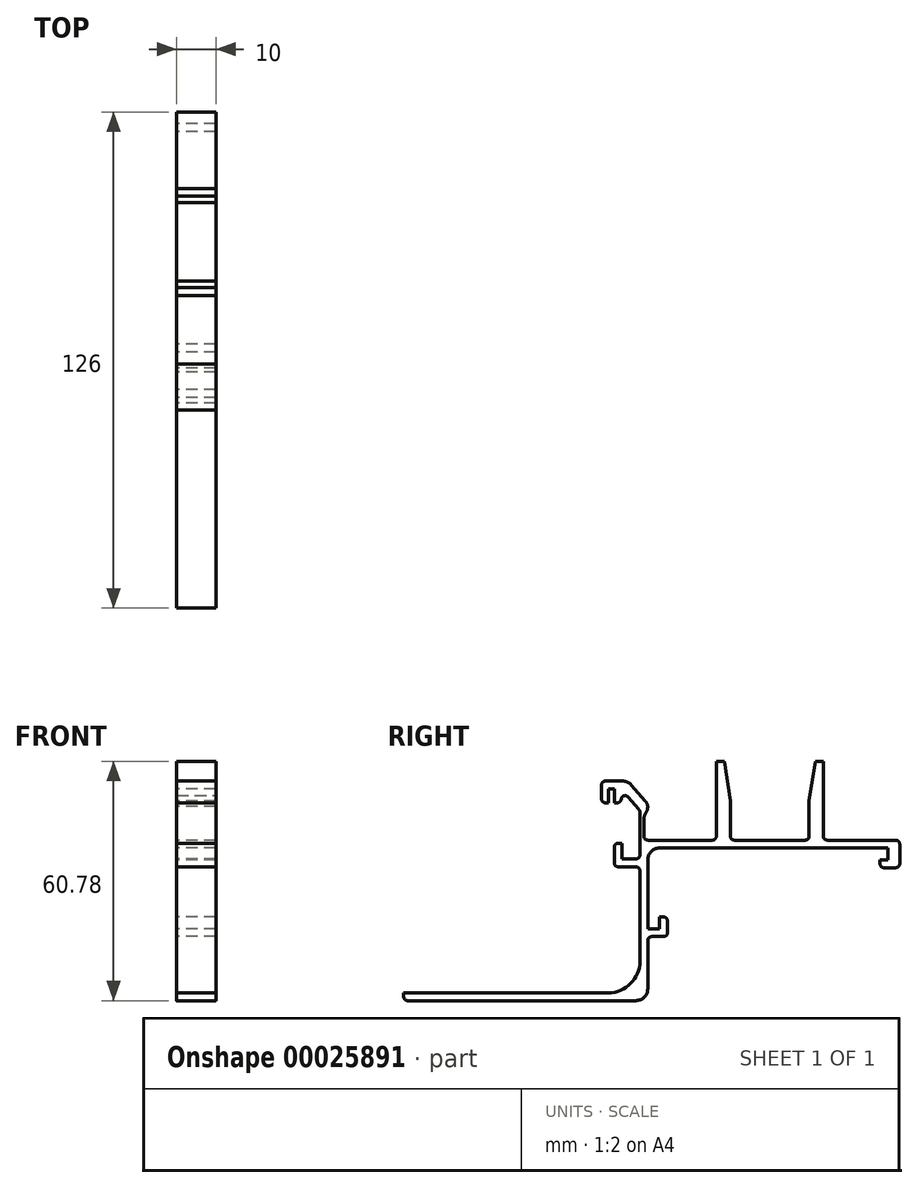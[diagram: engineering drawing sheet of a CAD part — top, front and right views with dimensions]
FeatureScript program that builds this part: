
annotation { "Feature Type Name" : "Feature", "Feature Type Description" : "" }
export const myFeature = defineFeature(function(context is Context, id is Id, definition is map)
    precondition{}
    {
        {
            var Q0;
            Q0=qCreatedBy(makeId("Right.planeOp"),FACE);
            var sketch = newSketch(context, id + "F0", { "sketchPlane" : qUnion([Q0])});
            skLineSegment(sketch, "E0", {"start": v(-5, 35.7) * mm, "end": v(56, 35.7) * mm});
            skLineSegment(sketch, "E1", {"start": v(56, 35.7) * mm, "end": v(56, 32.7) * mm});
            skLineSegment(sketch, "E2", {"start": v(56, 32.7) * mm, "end": v(54, 32.7) * mm});
            skLineSegment(sketch, "E3", {"start": v(54, 32.7) * mm, "end": v(54, 30.7) * mm});
            skLineSegment(sketch, "E4", {"start": v(54, 30.7) * mm, "end": v(59, 30.7) * mm});
            skLineSegment(sketch, "E5", {"start": v(59, 30.7) * mm, "end": v(59, 37.7) * mm});
            skLineSegment(sketch, "E6", {"start": v(59, 37.7) * mm, "end": v(-7, 37.7) * mm});
            skLineSegment(sketch, "E7", {"start": v(-5, 35.7) * mm, "end": v(-5, 15.2) * mm});
            skLineSegment(sketch, "E8", {"start": v(-7, 37.7) * mm, "end": v(-7, 17.59) * mm});
            skLineSegment(sketch, "E9", {"start": v(-5, 15.2) * mm, "end": v(-2, 15.2) * mm});
            skLineSegment(sketch, "E10", {"start": v(-2, 15.2) * mm, "end": v(-2, 18.2) * mm});
            skLineSegment(sketch, "E11", {"start": v(-2, 18.2) * mm, "end": v(0, 18.2) * mm});
            skLineSegment(sketch, "E12", {"start": v(0, 18.2) * mm, "end": v(0, 13.2) * mm});
            skLineSegment(sketch, "E13", {"start": v(0, 13.2) * mm, "end": v(-7, 13.2) * mm});
            skLineSegment(sketch, "E14", {"start": v(-7, 13.2) * mm, "end": v(-7, 17.59) * mm});
            skLineSegment(sketch, "E15", {"start": v(-5, 13.2) * mm, "end": v(-5, -3.82) * mm});
            skLineSegment(sketch, "E16", {"start": v(-7, -1.08) * mm, "end": v(-7, 13.2) * mm});
            skLineSegment(sketch, "E17", {"start": v(-7, 30.92) * mm, "end": v(-13.5, 30.92) * mm});
            skLineSegment(sketch, "E18", {"start": v(-13.5, 30.92) * mm, "end": v(-13.5, 36.92) * mm});
            skLineSegment(sketch, "E19", {"start": v(-13.5, 36.92) * mm, "end": v(-11.5, 36.92) * mm});
            skLineSegment(sketch, "E20", {"start": v(-11.5, 36.92) * mm, "end": v(-11.5, 32.92) * mm});
            skLineSegment(sketch, "E21", {"start": v(-11.5, 32.92) * mm, "end": v(-7, 32.92) * mm});
            skLineSegment(sketch, "E22", {"start": v(-7, -1.08) * mm, "end": v(-67, -1.08) * mm});
            skLineSegment(sketch, "E23", {"start": v(-5, -1.08) * mm, "end": v(-5, -3.82) * mm});
            skLineSegment(sketch, "E24", {"start": v(-67, -1.08) * mm, "end": v(-67, -3.08) * mm});
            skLineSegment(sketch, "E25", {"start": v(-67, -3.08) * mm, "end": v(-5, -3.08) * mm});
            skLineSegment(sketch, "E26", {"start": v(-5, -3.08) * mm, "end": v(-5, -1.08) * mm});
            skLineSegment(sketch, "E27", {"start": v(-62, -1.08) * mm, "end": v(-62, 4.95) * mm, "construction": true});
            skLineSegment(sketch, "E28", {"start": v(-7, 37.7) * mm, "end": v(-7, 49.25) * mm});
            skLineSegment(sketch, "E29", {"start": v(-8.26, 50.7) * mm, "end": v(-15, 50.7) * mm});
            skLineSegment(sketch, "E30", {"start": v(-15, 50.7) * mm, "end": v(-15, 47.2) * mm});
            skLineSegment(sketch, "E31", {"start": v(-15, 47.2) * mm, "end": v(-16.75, 47.2) * mm});
            skLineSegment(sketch, "E32", {"start": v(-16.75, 47.2) * mm, "end": v(-16.75, 52.7) * mm});
            skLineSegment(sketch, "E33", {"start": v(-16.75, 52.7) * mm, "end": v(-10, 52.7) * mm});
            skLineSegment(sketch, "E34", {"start": v(-7, 45.2) * mm, "end": v(-6, 45.2) * mm});
            skLineSegment(sketch, "E35", {"start": v(-6, 45.2) * mm, "end": v(-6, 37.7) * mm});
            skLineSegment(sketch, "E36", {"start": v(-5, 46.93) * mm, "end": v(-5, 45.2) * mm});
            skLineSegment(sketch, "E37", {"start": v(-5, 45.2) * mm, "end": v(-6, 45.2) * mm});
            skLineSegment(sketch, "E38", {"start": v(-11.75, 50.7) * mm, "end": v(-7, 45.2) * mm});
            skLineSegment(sketch, "E39", {"start": v(-7, 45.2) * mm, "end": v(-5, 46.93) * mm});
            skLineSegment(sketch, "E40", {"start": v(-5, 46.93) * mm, "end": v(-10, 52.7) * mm});
            skPoint(sketch, "E41.start.orphan", {"position": v(-7, 52.7) * mm});
            skLineSegment(sketch, "E42", {"start": v(-13.5, 50.7) * mm, "end": v(-13.5, 47.2) * mm});
            skLineSegment(sketch, "E43", {"start": v(-13.5, 47.2) * mm, "end": v(-11.75, 47.2) * mm});
            skLineSegment(sketch, "E44", {"start": v(-11.75, 47.2) * mm, "end": v(-11.75, 50.7) * mm});
            skLineSegment(sketch, "E45", {"start": v(26, 37.7) * mm, "end": v(26, 54.51) * mm, "construction": true});
            skLineSegment(sketch, "E46", {"start": v(16, 37.7) * mm, "end": v(16, 47.7) * mm});
            skLineSegment(sketch, "E47", {"start": v(16, 47.7) * mm, "end": v(14.42, 57.7) * mm});
            skLineSegment(sketch, "E48", {"start": v(14.42, 57.7) * mm, "end": v(12.42, 57.7) * mm});
            skLineSegment(sketch, "E49", {"start": v(12.42, 57.7) * mm, "end": v(12.42, 37.7) * mm});
            skLineSegment(sketch, "E50.MirrorCS", {"start": v(37.58, 57.7) * mm, "end": v(39.58, 57.7) * mm});
            skLineSegment(sketch, "E51.MirrorCS", {"start": v(36, 37.7) * mm, "end": v(36, 47.7) * mm});
            skLineSegment(sketch, "E52.MirrorCS", {"start": v(36, 47.7) * mm, "end": v(37.58, 57.7) * mm});
            skLineSegment(sketch, "E53.MirrorCS", {"start": v(39.58, 57.7) * mm, "end": v(39.58, 37.7) * mm});
            skSolve(sketch);
        }
        {
            var Q0;
            Q0=qSketchRegion(id+"F0",true);
            extrude(context, id + "F1", {"entities" : qUnion([Q0]), "depth" : 10 * mm});
        }
        {
            var Q0;
            Q0=makeQuery(id+"F1.opExtrude","SWEPT_EDGE",EDGE,{"disambiguationData":[OSD([sQuery(id+"F0.wireOp",EDGE,"E0"),sQuery(id+"F0.wireOp",EDGE,"E7")])]});
            fillet(context, id + "F2", {"entities" : qUnion([Q0]), "radius" : 3 * mm, "tangentPropagation" : true, "allowEdgeOverflow" : false});
        }
        {
            var Q0;
            Q0=makeQuery(id+"F1.opExtrude","SWEPT_EDGE",EDGE,{"disambiguationData":[OSD([sQuery(id+"F0.wireOp",EDGE,"E6"),sQuery(id+"F0.wireOp",EDGE,"E8")])]});
            var Q1;
            Q1=makeQuery(id+"F1.opExtrude","SWEPT_EDGE",EDGE,{"disambiguationData":[OSD([sQuery(id+"F0.wireOp",EDGE,"E13"),sQuery(id+"F0.wireOp",EDGE,"E14")])]});
            var Q2;
            Q2=makeQuery(id+"F1.opExtrude","SWEPT_EDGE",EDGE,{"disambiguationData":[OSD([sQuery(id+"F0.wireOp",EDGE,"E12"),sQuery(id+"F0.wireOp",EDGE,"E13")])]});
            var Q3;
            Q3=makeQuery(id+"F1.opExtrude","SWEPT_EDGE",EDGE,{"disambiguationData":[OSD([sQuery(id+"F0.wireOp",EDGE,"E5"),sQuery(id+"F0.wireOp",EDGE,"E6")])]});
            var Q4;
            Q4=makeQuery(id+"F1.opExtrude","SWEPT_EDGE",EDGE,{"disambiguationData":[OSD([sQuery(id+"F0.wireOp",EDGE,"E4"),sQuery(id+"F0.wireOp",EDGE,"E5")])]});
            var Q5;
            Q5=makeQuery(id+"F1.opExtrude","SWEPT_EDGE",EDGE,{"disambiguationData":[OSD([sQuery(id+"F0.wireOp",EDGE,"E3"),sQuery(id+"F0.wireOp",EDGE,"E4")])]});
            var Q6;
            Q6=makeQuery(id+"F1.opExtrude","SWEPT_EDGE",EDGE,{"disambiguationData":[OSD([sQuery(id+"F0.wireOp",EDGE,"E11"),sQuery(id+"F0.wireOp",EDGE,"E12")])]});
            fillet(context, id + "F3", {"entities" : qUnion([Q0, Q1, Q2, Q3, Q4, Q5, Q6]), "radius" : 1 * mm, "tangentPropagation" : true, "allowEdgeOverflow" : false});
        }
        {
            var Q0;
            Q0=makeQuery(id+"F1.opExtrude","SWEPT_EDGE",EDGE,{"disambiguationData":[OSD([sQuery(id+"F0.wireOp",EDGE,"E16"),sQuery(id+"F0.wireOp",EDGE,"E22")])]});
            fillet(context, id + "F4", {"entities" : qUnion([Q0]), "radius" : 8 * mm, "tangentPropagation" : true, "allowEdgeOverflow" : false});
        }
        {
            var Q0;
            Q0=makeQuery(id+"F1.opExtrude","SWEPT_EDGE",EDGE,{"disambiguationData":[OSD([sQuery(id+"F0.wireOp",EDGE,"E24"),sQuery(id+"F0.wireOp",EDGE,"E25")])]});
            var Q1;
            Q1=makeQuery(id+"F1.opExtrude","SWEPT_EDGE",EDGE,{"disambiguationData":[OSD([sQuery(id+"F0.wireOp",EDGE,"E17"),sQuery(id+"F0.wireOp",EDGE,"E18")])]});
            var Q2;
            Q2=makeQuery(id+"F1.opExtrude","SWEPT_EDGE",EDGE,{"disambiguationData":[OSD([sQuery(id+"F0.wireOp",EDGE,"E8"),sQuery(id+"F0.wireOp",EDGE,"E21")])]});
            var Q3;
            Q3=makeQuery(id+"F1.opExtrude","SWEPT_EDGE",EDGE,{"disambiguationData":[OSD([sQuery(id+"F0.wireOp",EDGE,"E8"),sQuery(id+"F0.wireOp",EDGE,"E17")])]});
            fillet(context, id + "F5", {"entities" : qUnion([Q0, Q1, Q2, Q3]), "radius" : 1 * mm, "tangentPropagation" : true, "allowEdgeOverflow" : false});
        }
        {
            var Q0;
            Q0=makeQuery(id+"F1.opExtrude","SWEPT_EDGE",EDGE,{"disambiguationData":[OSD([sQuery(id+"F0.wireOp",EDGE,"E25"),sQuery(id+"F0.wireOp",EDGE,"E26")])]});
            fillet(context, id + "F6", {"entities" : qUnion([Q0]), "radius" : 3 * mm, "tangentPropagation" : true, "allowEdgeOverflow" : false});
        }
        {
            var Q0;
            Q0=makeQuery(id+"F1.opExtrude","SWEPT_EDGE",EDGE,{"disambiguationData":[OSD([sQuery(id+"F0.wireOp",EDGE,"E34"),sQuery(id+"F0.wireOp",EDGE,"E35"),sQuery(id+"F0.wireOp",EDGE,"E37")])]});
            fillet(context, id + "F7", {"entities" : qUnion([Q0]), "radius" : 3 * mm, "tangentPropagation" : true, "allowEdgeOverflow" : false});
        }
        {
            var Q0;
            Q0=makeQuery(id+"F7.opFillet","BLEND_EDGE",EDGE,{"blendedFrom":[makeQuery(id+"F1.opExtrude","SWEPT_EDGE",EDGE,{"disambiguationData":[OSD([sQuery(id+"F0.wireOp",EDGE,"E34"),sQuery(id+"F0.wireOp",EDGE,"E35"),sQuery(id+"F0.wireOp",EDGE,"E37")])]}),makeQuery(id+"F1.opExtrude","SWEPT_FACE",FACE,{"disambiguationData":[OSD([sQuery(id+"F0.wireOp",EDGE,"E36")])]})],"blendedInto":[makeQuery(id+"F1.opExtrude","SWEPT_FACE",FACE,{"disambiguationData":[OSD([sQuery(id+"F0.wireOp",EDGE,"E36")])]})]});
            fillet(context, id + "F8", {"entities" : qUnion([Q0]), "radius" : 3 * mm, "tangentPropagation" : true, "allowEdgeOverflow" : false});
        }
        {
            var Q0;
            Q0=makeQuery(id+"F1.opExtrude","SWEPT_EDGE",EDGE,{"disambiguationData":[OSD([sQuery(id+"F0.wireOp",EDGE,"E41"),sQuery(id+"F0.wireOp",EDGE,"E36")])]});
            var Q1;
            Q1=makeQuery(id+"F1.opExtrude","SWEPT_EDGE",EDGE,{"disambiguationData":[OSD([sQuery(id+"F0.wireOp",EDGE,"E32"),sQuery(id+"F0.wireOp",EDGE,"E33")])]});
            var Q2;
            Q2=makeQuery(id+"F1.opExtrude","SWEPT_EDGE",EDGE,{"disambiguationData":[OSD([sQuery(id+"F0.wireOp",EDGE,"E31"),sQuery(id+"F0.wireOp",EDGE,"E32")])]});
            var Q3;
            Q3=makeQuery(id+"F1.opExtrude","SWEPT_EDGE",EDGE,{"disambiguationData":[OSD([sQuery(id+"F0.wireOp",EDGE,"E18"),sQuery(id+"F0.wireOp",EDGE,"E19")])]});
            fillet(context, id + "F9", {"entities" : qUnion([Q0, Q1, Q2, Q3]), "radius" : 1 * mm, "tangentPropagation" : true, "allowEdgeOverflow" : false});
        }
        {
            var Q0;
            Q0=makeQuery(id+"F1.opExtrude","SWEPT_EDGE",EDGE,{"disambiguationData":[OSD([sQuery(id+"F0.wireOp",EDGE,"E29"),sQuery(id+"F0.wireOp",EDGE,"E38"),sQuery(id+"F0.wireOp",EDGE,"E44")])]});
            fillet(context, id + "F10", {"entities" : qUnion([Q0]), "radius" : 1 * mm, "tangentPropagation" : true, "allowEdgeOverflow" : false});
        }
        {
            var Q0;
            Q0=makeQuery(id+"F1.opExtrude","SWEPT_EDGE",EDGE,{"disambiguationData":[OSD([sQuery(id+"F0.wireOp",EDGE,"E36"),sQuery(id+"F0.wireOp",EDGE,"E39"),sQuery(id+"F0.wireOp",EDGE,"E40")])]});
            fillet(context, id + "F11", {"entities" : qUnion([Q0]), "radius" : 3 * mm, "tangentPropagation" : true, "allowEdgeOverflow" : false});
        }
        {
            var Q0;
            Q0=makeQuery(id+"F1.opExtrude","SWEPT_EDGE",EDGE,{"disambiguationData":[OSD([sQuery(id+"F0.wireOp",EDGE,"E33"),sQuery(id+"F0.wireOp",EDGE,"E40")])]});
            fillet(context, id + "F12", {"entities" : qUnion([Q0]), "radius" : 3 * mm, "tangentPropagation" : true, "allowEdgeOverflow" : false});
        }
        {
            var Q0;
            Q0=makeQuery(id+"F1.opExtrude","SWEPT_EDGE",EDGE,{"disambiguationData":[OSD([sQuery(id+"F0.wireOp",EDGE,"E43"),sQuery(id+"F0.wireOp",EDGE,"E44")])]});
            var Q1;
            Q1=makeQuery(id+"F1.opExtrude","SWEPT_EDGE",EDGE,{"disambiguationData":[OSD([sQuery(id+"F0.wireOp",EDGE,"E28"),sQuery(id+"F0.wireOp",EDGE,"E34"),sQuery(id+"F0.wireOp",EDGE,"E38"),sQuery(id+"F0.wireOp",EDGE,"E39")])]});
            fillet(context, id + "F13", {"entities" : qUnion([Q0, Q1]), "radius" : 1 * mm, "tangentPropagation" : true, "allowEdgeOverflow" : false});
        }
    });
